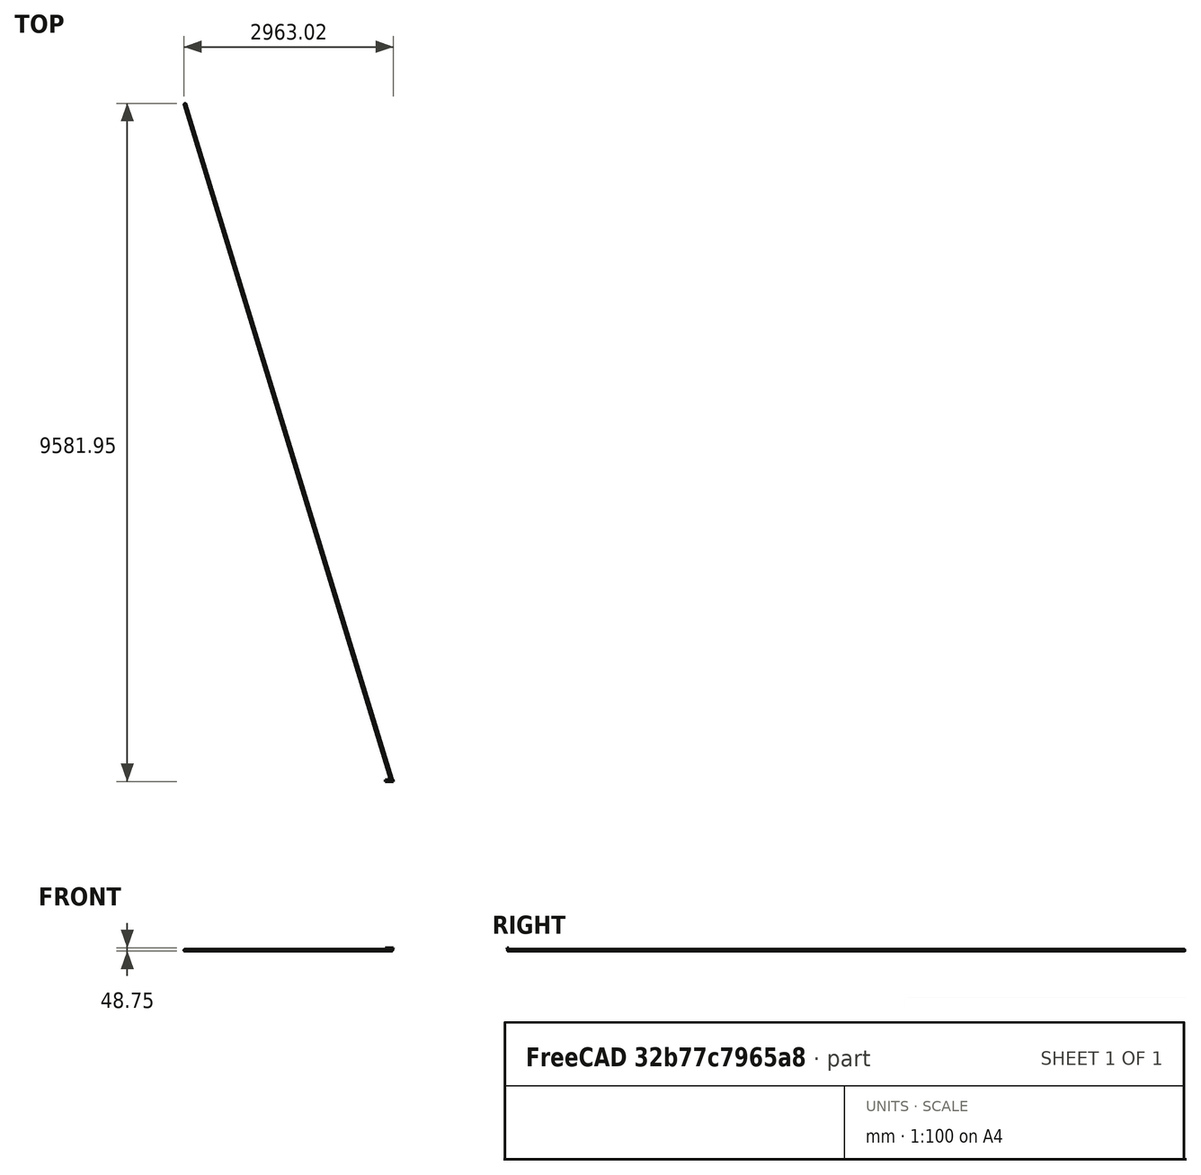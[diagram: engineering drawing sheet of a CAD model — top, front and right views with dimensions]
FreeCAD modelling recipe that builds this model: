
FCSTD DOCUMENT  (FreeCAD 0.16R)
Label: Guide8
License: All rights reserved
LicenseURL: http://en.wikipedia.org/wiki/All_rights_reserved
objects: Sketcher::SketchObject×8, PartDesign::Pocket×6, PartDesign::Chamfer×4, PartDesign::Pad×2, PartDesign::Fillet×2, Mesh::Feature×1
note: 30 computed .brp shape members not serialized (recipe doc carries the construction recipe); baked Part::Feature solids carry a one-line shape summary decoded from their .brp

FEATURE [Sketcher::SketchObject] Sketch
  sketch-geometry (4):
    g0: LineSegment StartX=-60 StartY=0 StartZ=0 EndX=0 EndY=0 EndZ=0
    g1: LineSegment StartX=0 StartY=0 StartZ=0 EndX=0 EndY=-30 EndZ=0
    g2: LineSegment StartX=0 StartY=-30 StartZ=0 EndX=-60 EndY=-30 EndZ=0
    g3: LineSegment StartX=-60 StartY=-30 StartZ=0 EndX=-60 EndY=0 EndZ=0
  constraints (11):
    c: Coincident(g0,g1)
    c: Coincident(g1,g2)
    c: Coincident(g2,g3)
    c: Coincident(g3,g0)
    c: Horizontal(g0)
    c: Horizontal(g2)
    c: Vertical(g1)
    c: Vertical(g3)
    c: Coincident(g0,g-1)
    c: Distance(g3) = 30
    c: Distance(g0) = 60
FEATURE [PartDesign::Pad] Pad
  Length = 12
  Length2 = 100
  Midplane = true
  Sketch = -> Sketch
  Type = 0
FEATURE [Sketcher::SketchObject] Sketch001
  Placement = pos=(0,-30,0) rot=(1,0,0;1.5708rad)
  Support = -> Pad [Face3]
  sketch-geometry (4):
    g0: LineSegment StartX=-95.8323 StartY=4.5 StartZ=0 EndX=18.8197 EndY=4.5 EndZ=0
    g1: LineSegment StartX=18.8197 StartY=4.5 StartZ=0 EndX=18.8197 EndY=-4.5 EndZ=0
    g2: LineSegment StartX=18.8197 StartY=-4.5 StartZ=0 EndX=-95.8323 EndY=-4.5 EndZ=0
    g3: LineSegment StartX=-95.8323 StartY=-4.5 StartZ=0 EndX=-95.8323 EndY=4.5 EndZ=0
  constraints (12):
    c: Coincident(g0,g1)
    c: Coincident(g1,g2)
    c: Coincident(g2,g3)
    c: Coincident(g3,g0)
    c: Horizontal(g0)
    c: Horizontal(g2)
    c: Vertical(g1)
    c: Vertical(g3)
    c: DistanceX(g1) = 18.8197
    c: DistanceX(g2) = -95.8323
    c: Symmetric(g1,g0,g-1)
    c: Distance(g1) = 9
FEATURE [PartDesign::Pocket] Pocket
  Length = 24
  Sketch = -> Sketch001
  Type = 0
FEATURE [Sketcher::SketchObject] Sketch003
  ExternalGeometry = -> [Pocket]
  Placement = pos=(0,0,-6) rot=(1,0,0;3.14159rad)
  Support = -> Pocket [Face4]
  sketch-geometry (7):
    g0: LineSegment StartX=-31.6449 StartY=0 StartZ=0 EndX=6 EndY=0 EndZ=0
    g1: LineSegment StartX=6 StartY=0 StartZ=0 EndX=8.92372 EndY=9.56305 EndZ=0
    g2: LineSegment StartX=8.92372 StartY=9.56305 StartZ=0 EndX=-25.5033 EndY=20.0884 EndZ=0
    g3: LineSegment StartX=-25.5033 StartY=20.0884 StartZ=0 EndX=-31.6449 EndY=0 EndZ=0
    g4: LineSegment [constr] StartX=0.884158 StartY=44.8323 StartZ=0 EndX=-19.2182 EndY=-20.9195 EndZ=0
    g5: LineSegment StartX=-31.6449 StartY=0 StartZ=0 EndX=6 EndY=0 EndZ=0
    g6: LineSegment StartX=-31.6449 StartY=0 StartZ=0 EndX=6 EndY=0 EndZ=0
  constraints (21):
    c: Horizontal(g0)
    c: Coincident(g0,g1)
    c: Coincident(g1,g2)
    c: Coincident(g2,g3)
    c: Coincident(g3,g0)
    c: Parallel(g1,g3)
    c: Perpendicular(g3,g2)
    c: Distance(g2) = 36
    c: PointOnObject(g0,g-3)
    c: Perpendicular(g4,g2)
    c: Symmetric(g1,g2,g4)
    c: Distance(g1) = 10
    c: Angle(g4) = -1.8675
    c: DistanceX(g0) = 6
    c: Distance(g4) = 68.7561
    c: DistanceY(g4) = 44.8323
    c: Coincident(g5,g0)
    c: PointOnObject(g5,g-1)
    c: Coincident(g6,g0)
    c: Coincident(g6,g5)
    c: Coincident(g5,g0)
FEATURE [PartDesign::Pad] Pad001
  Length = 24
  Length2 = 100
  Sketch = -> Sketch003
  Type = 0
FEATURE [Sketcher::SketchObject] Sketch004
  ExternalGeometry = -> [Pad001]
  Placement = pos=(3.4366,-11.2406,0) rot=(0.978386,0.146221,0.146221;1.59265rad)
  Support = -> Pad001 [Face11]
  sketch-geometry (1):
    g0: Circle CenterX=-12.2622 CenterY=-30 CenterZ=0 NormalX=0 NormalY=0 NormalZ=1 Radius=12.75
  constraints (2):
    c: Radius(g0) = 12.75
    c: Symmetric(g-3,g-3,g0)
FEATURE [PartDesign::Pocket] Pocket001
  Length = 5
  Sketch = -> Sketch004
  Type = 1
FEATURE [Sketcher::SketchObject] Sketch005
  Placement = pos=(0,0,6) rot=(0,0,1;0rad)
  Support = -> Pocket001 [Face4]
  sketch-geometry (1):
    g0: Circle CenterX=0 CenterY=-70 CenterZ=0 NormalX=0 NormalY=0 NormalZ=1 Radius=60
  constraints (3):
    c: Radius(g0) = 60
    c: PointOnObject(g0,g-2)
    c: DistanceY(g0) = -70
FEATURE [PartDesign::Pocket] Pocket002
  Length = 13
  Sketch = -> Sketch005
  Type = 0
FEATURE [PartDesign::Fillet] Fillet
  Base = -> Pocket002 [Edge4,Edge8,Edge19,Edge29,Edge45,Edge2]
  Radius = 5
FEATURE [PartDesign::Chamfer] Chamfer
  Base = -> Fillet [Edge27]
  Size = 1
FEATURE [PartDesign::Fillet] Fillet001
  Base = -> Chamfer [Edge82]
  Radius = 5
FEATURE [PartDesign::Chamfer] Chamfer001
  Base = -> Fillet001 [Edge46]
  Size = 1
FEATURE [PartDesign::Chamfer] Chamfer002
  Base = -> Chamfer001 [Edge23]
  Size = 1
FEATURE [PartDesign::Chamfer] Chamfer003
  Base = -> Chamfer002 [Edge13]
  Size = 1
FEATURE [Sketcher::SketchObject] Sketch006
  ExternalGeometry = -> [Chamfer003]
  Placement = pos=(0,0,-30) rot=(1,0,0;3.14159rad)
  Support = -> Chamfer003 [Face6]
  sketch-geometry (2):
    g0: Circle CenterX=-24.4681 CenterY=14.0684 CenterZ=0 NormalX=0 NormalY=0 NormalZ=1 Radius=1.9
    g1: Circle CenterX=4.69918 CenterY=5.15104 CenterZ=0 NormalX=0 NormalY=0 NormalZ=1 Radius=1.9
  constraints (6):
    c: Radius(g1) = 1.9
    c: Equal(g1,g0)
    c: Distance(g1,g-6) = 2.5
    c: Distance(g0,g-5) = 2.5
    c: Distance(g-5,g0) = 6
    c: Distance(g1,g-6) = 6
FEATURE [PartDesign::Pocket] Pocket003
  Length = 12
  Sketch = -> Sketch006
  Type = 0
FEATURE [Sketcher::SketchObject] Sketch007
  ExternalGeometry = -> [Pocket003]
  Placement = pos=(-28.9399,-8.8478,0) rot=(0.690875,-0.51122,-0.51122;1.93244rad)
  Support = -> Pocket003 [Face12]
  sketch-geometry (5):
    g0: LineSegment StartX=3.55423 StartY=-21 StartZ=0 EndX=9.35423 EndY=-21 EndZ=0
    g1: LineSegment StartX=9.35423 StartY=-21 StartZ=0 EndX=9.35423 EndY=-24 EndZ=0
    g2: LineSegment StartX=9.35423 StartY=-24 StartZ=0 EndX=3.55423 EndY=-24 EndZ=0
    g3: LineSegment StartX=3.55423 StartY=-24 StartZ=0 EndX=3.55423 EndY=-21 EndZ=0
    g4: LineSegment [constr] StartX=6.45423 StartY=-21 StartZ=0 EndX=6.45423 EndY=-34.5521 EndZ=0
  constraints (15):
    c: Coincident(g0,g1)
    c: Coincident(g1,g2)
    c: Coincident(g2,g3)
    c: Coincident(g3,g0)
    c: Horizontal(g0)
    c: Horizontal(g2)
    c: Vertical(g1)
    c: Vertical(g3)
    c: Distance(g2) = 5.8
    c: Distance(g1) = 3
    c: Vertical(g4)
    c: Symmetric(g0,g0,g4)
    c: PointOnObject(g4,g0)
    c: Distance(g-4,g4) = 5.3
    c: DistanceY(g1) = -24
FEATURE [PartDesign::Pocket] Pocket004
  Length = 6
  Sketch = -> Sketch007
  Type = 0
FEATURE [Sketcher::SketchObject] Sketch008
  ExternalGeometry = -> [Pocket003]
  Placement = pos=(5.48711,1.67758,0) rot=(0.463605,0.626526,0.626526;2.27337rad)
  Support = -> Pocket004 [Face21]
  sketch-geometry (5):
    g0: LineSegment StartX=-9.45427 StartY=-20 StartZ=0 EndX=-3.45427 EndY=-20 EndZ=0
    g1: LineSegment StartX=-3.45427 StartY=-20 StartZ=0 EndX=-3.45427 EndY=-23 EndZ=0
    g2: LineSegment StartX=-3.45427 StartY=-23 StartZ=0 EndX=-9.45427 EndY=-23 EndZ=0
    g3: LineSegment StartX=-9.45427 StartY=-23 StartZ=0 EndX=-9.45427 EndY=-20 EndZ=0
    g4: LineSegment [constr] StartX=-6.45427 StartY=-20 StartZ=0 EndX=-6.45427 EndY=-30.0211 EndZ=0
  constraints (15):
    c: Coincident(g0,g1)
    c: Coincident(g1,g2)
    c: Coincident(g2,g3)
    c: Coincident(g3,g0)
    c: Horizontal(g0)
    c: Horizontal(g2)
    c: Vertical(g1)
    c: Vertical(g3)
    c: Distance(g2) = 6
    c: Distance(g1) = 3
    c: Vertical(g4)
    c: Symmetric(g0,g0,g4)
    c: PointOnObject(g4,g0)
    c: Distance(g4,g-4) = 5.3
    c: DistanceY(g0) = -20
FEATURE [PartDesign::Pocket] Pocket005
  Length = 6
  Sketch = -> Sketch008
  Type = 0
FEATURE [Mesh::Feature] Mesh  label="Pocket005 (Meshed)"
